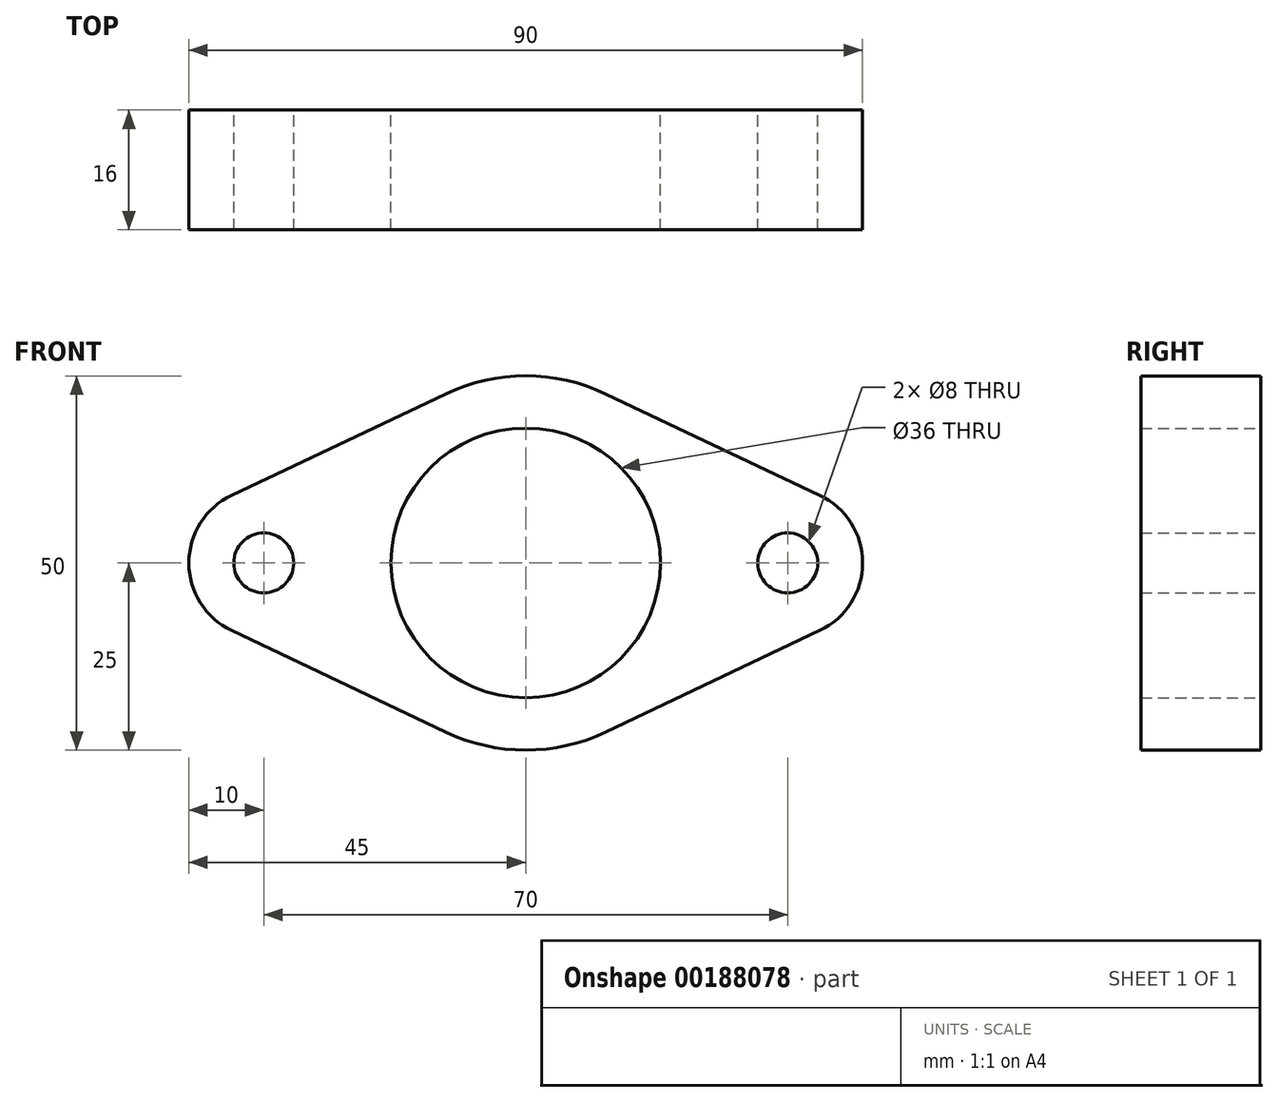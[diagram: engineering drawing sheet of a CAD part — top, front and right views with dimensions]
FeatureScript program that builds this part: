
annotation { "Feature Type Name" : "Feature", "Feature Type Description" : "" }
export const myFeature = defineFeature(function(context is Context, id is Id, definition is map)
    precondition{}
    {
        {
            var Q0;
            Q0=qCreatedBy(makeId("Front.planeOp"),FACE);
            var sketch = newSketch(context, id + "F0", { "sketchPlane" : qUnion([Q0])});
            skCircle(sketch, "E0", {"center": v(0, 0) * mm, "radius": 18 * mm});
            skArc(sketch, "E1", {"start": v(-10.71, -22.59) * mm, "mid": v(0, -25) * mm, "end": v(10.71, -22.59) * mm});
            skLineSegment(sketch, "E2", {"start": v(0, 0) * mm, "end": v(35, 0) * mm, "construction": true});
            skArc(sketch, "E3", {"start": v(39.29, -9.04) * mm, "mid": v(45, 0) * mm, "end": v(39.29, 9.04) * mm});
            skLineSegment(sketch, "E4", {"start": v(0, 0) * mm, "end": v(-35, 0) * mm, "construction": true});
            skArc(sketch, "E5", {"start": v(-39.29, 9.04) * mm, "mid": v(-45, 0) * mm, "end": v(-39.29, -9.04) * mm});
            skLineSegment(sketch, "E6", {"start": v(-39.29, 9.04) * mm, "end": v(-10.71, 22.59) * mm});
            skLineSegment(sketch, "E7", {"start": v(10.71, 22.59) * mm, "end": v(39.29, 9.04) * mm});
            skLineSegment(sketch, "E8", {"start": v(-39.29, -9.04) * mm, "end": v(-10.71, -22.59) * mm});
            skLineSegment(sketch, "E9", {"start": v(10.71, -22.59) * mm, "end": v(39.29, -9.04) * mm});
            skArc(sketch, "E10.trimOffspring", {"start": v(10.71, 22.59) * mm, "mid": v(0, 25) * mm, "end": v(-10.71, 22.59) * mm});
            skSolve(sketch);
        }
        {
            var Q0;
            Q0=qSketchRegion(id+"F0",true);
            extrude(context, id + "F1", {"entities" : qUnion([Q0]), "depth" : 16 * mm});
        }
        {
            var Q0;
            Q0=sQuery(id+"F0.wireOp",VERTEX,"E3.center");
            var Q1;
            Q1=sQuery(id+"F0.wireOp",VERTEX,"E5.center");
            var Q2;
            Q2=makeQuery(id+"F1.opExtrude","SWEPT_BODY",BODY,{"disambiguationData":[OSD([sQuery(id+"F0.wireOp",EDGE,"E0"),sQuery(id+"F0.wireOp",EDGE,"E1"),sQuery(id+"F0.wireOp",EDGE,"E3"),sQuery(id+"F0.wireOp",EDGE,"E5"),sQuery(id+"F0.wireOp",EDGE,"E6"),sQuery(id+"F0.wireOp",EDGE,"E7"),sQuery(id+"F0.wireOp",EDGE,"E8"),sQuery(id+"F0.wireOp",EDGE,"E9"),sQuery(id+"F0.wireOp",EDGE,"E10.trimOffspring")])]});
            hole(context, id + "F2", {"style" : HoleStyle.SIMPLE, "endStyle" : HoleEndStyle.THROUGH, "oppositeDirection" : true, "holeDiameter" : 8 * mm, "locations" : qUnion([Q0, Q1]), "scope" : qUnion([Q2]), "isTappedThrough" : true});
        }
    });
